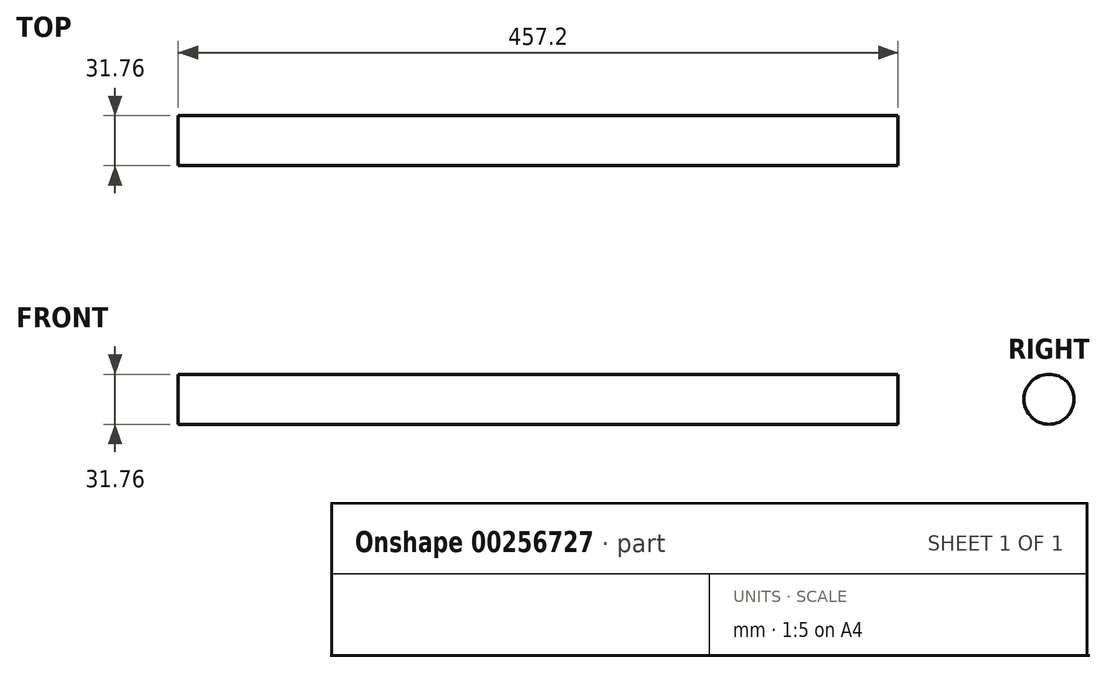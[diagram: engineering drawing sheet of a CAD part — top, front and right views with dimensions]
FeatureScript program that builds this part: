
annotation { "Feature Type Name" : "Feature", "Feature Type Description" : "" }
export const myFeature = defineFeature(function(context is Context, id is Id, definition is map)
    precondition{}
    {
        {
            var Q0;
            Q0=qCreatedBy(makeId("Right.planeOp"),FACE);
            var sketch = newSketch(context, id + "F0", { "sketchPlane" : qUnion([Q0])});
            skCircle(sketch, "E0", {"center": v(0, 0) * mm, "radius": 15.88 * mm});
            skSolve(sketch);
        }
        {
            var Q0;
            Q0=makeQuery(id+"F0.imprint","IMPRINT",FACE,{"disambiguationData":[TD([[makeQuery(id+"F0.imprint","IMPRINT",EDGE,{"derivedFrom":sQuery(id+"F0.wireOp",EDGE,"E0")}),1.0]])]});
            extrude(context, id + "F1", {"entities" : qUnion([Q0]), "depth" : 457.2 * mm});
        }
    });
